# Revit family: 634-00-001 DN200-250
name_source: partatom
category: Pipe Accessories
units: mm (PartAtom-declared; Revit-internal decimal feet)

## family parameters
Always vertical = Yes
Cut with Voids When Loaded = No
Part Type = Valve - Breaks Into
Round Connector Dimension = Use Diameter
Shared = No
Work Plane-Based = No

## types (6) — shared parameters
10 = 10 mm  [stored 0.0328084 ft]
2 = 2 mm  [stored 0.00656168 ft]
Bolt_L = 65 mm  [stored 0.213255 ft]
D2 = 41 mm  [stored 0.134514 ft]
D2_L = 81 mm  [stored 0.265748 ft]
DN200_PN16_AVK ref. no. 634-227-00-016 = 634-227-00-016
DN200_PN16_AVK ref. no. 634-227-00-036 = 634-227-00-036
DN225_PN16_AVK ref. no. 634-257-00-016 = 634-257-00-016
DN225_PN16_AVK ref. no. 634-257-00-036 = 634-257-00-036
DN250_PN16_AVK ref. no. 634-301-00-016 = 634-301-00-016
DN250_PN16_AVK ref. no. 634-301-00-036 = 634-301-00-036
Description_ = AVK SUPA MAXI™ END CAP, PN16
L-L1 = 41 mm  [stored 0.134514 ft]
Nut = 16 mm
Search_table = 634-00-001 DN200-250
URL product pages = https://www.avkvalves.com
zero-valued in all types: Default Elevation, Thickness

## per-type parameters (varying)
| type | Bore | D | D-10 | D1 | D11 | D12 | D1_L | DN | FL_T | L | L1 | Radius | S1 | S2 |
| DN200_PN16_AVK ref. no. 634-227-00-016 | 100 mm  [stored 0.328084 ft] | 195 mm  [stored 0.639764 ft] | 185 mm | 125 mm  [stored 0.410105 ft] | 156 mm | 10 mm  [stored 0.0328084 ft] | 65 mm  [stored 0.213255 ft] | 200 mm  [stored 0.656168 ft] | 20 mm  [stored 0.0656168 ft] | 130 mm  [stored 0.426509 ft] | 65 mm  [stored 0.213255 ft] | 25 mm  [stored 0.082021 ft] | 97 mm | 114 mm |
| DN200_PN16_AVK ref. no. 634-227-00-036 | 100 mm  [stored 0.328084 ft] | 195 mm  [stored 0.639764 ft] | 185 mm | 125 mm  [stored 0.410105 ft] | 156 mm | 10 mm  [stored 0.0328084 ft] | 65 mm  [stored 0.213255 ft] | 200 mm  [stored 0.656168 ft] | 20 mm  [stored 0.0656168 ft] | 130 mm  [stored 0.426509 ft] | 65 mm  [stored 0.213255 ft] | 25 mm  [stored 0.082021 ft] | 97 mm | 114 mm |
| DN225_PN16_AVK ref. no. 634-257-00-016 | 113 mm | 219 mm | 209 mm | 141 mm | 175 mm | 12 mm  [stored 0.0393701 ft] | 81 mm  [stored 0.265748 ft] | 225 mm | 20 mm  [stored 0.0656168 ft] | 139 mm | 69 mm  [stored 0.226378 ft] | 30 mm  [stored 0.0984252 ft] | 112 mm  [stored 0.367454 ft] | 129 mm |
| DN225_PN16_AVK ref. no. 634-257-00-036 | 113 mm | 219 mm | 209 mm | 141 mm | 175 mm | 12 mm  [stored 0.0393701 ft] | 81 mm  [stored 0.265748 ft] | 225 mm | 20 mm  [stored 0.0656168 ft] | 139 mm | 69 mm  [stored 0.226378 ft] | 30 mm  [stored 0.0984252 ft] | 112 mm  [stored 0.367454 ft] | 129 mm |
| DN250_PN16_AVK ref. no. 634-301-00-016 | 125 mm  [stored 0.410105 ft] | 238 mm | 228 mm  [stored 0.748031 ft] | 163 mm | 190 mm | 13 mm  [stored 0.0426509 ft] | 81 mm  [stored 0.265748 ft] | 250 mm | 22 mm  [stored 0.0721785 ft] | 136 mm | 68 mm  [stored 0.223097 ft] | 33 mm  [stored 0.108268 ft] | 133 mm  [stored 0.436352 ft] | 151 mm |
| DN250_PN16_AVK ref. no. 634-301-00-036 | 125 mm  [stored 0.410105 ft] | 238 mm | 228 mm  [stored 0.748031 ft] | 163 mm | 190 mm | 13 mm  [stored 0.0426509 ft] | 81 mm  [stored 0.265748 ft] | 250 mm | 22 mm  [stored 0.0721785 ft] | 136 mm | 68 mm  [stored 0.223097 ft] | 33 mm  [stored 0.108268 ft] | 133 mm  [stored 0.436352 ft] | 151 mm |

note: [stored X ft] marks values corroborated as IEEE doubles in the binary element streams (Revit-internal decimal feet)

## geometry (parser evidence)
native form markers: Sweep x3
no freeform markers — native parametric forms only
